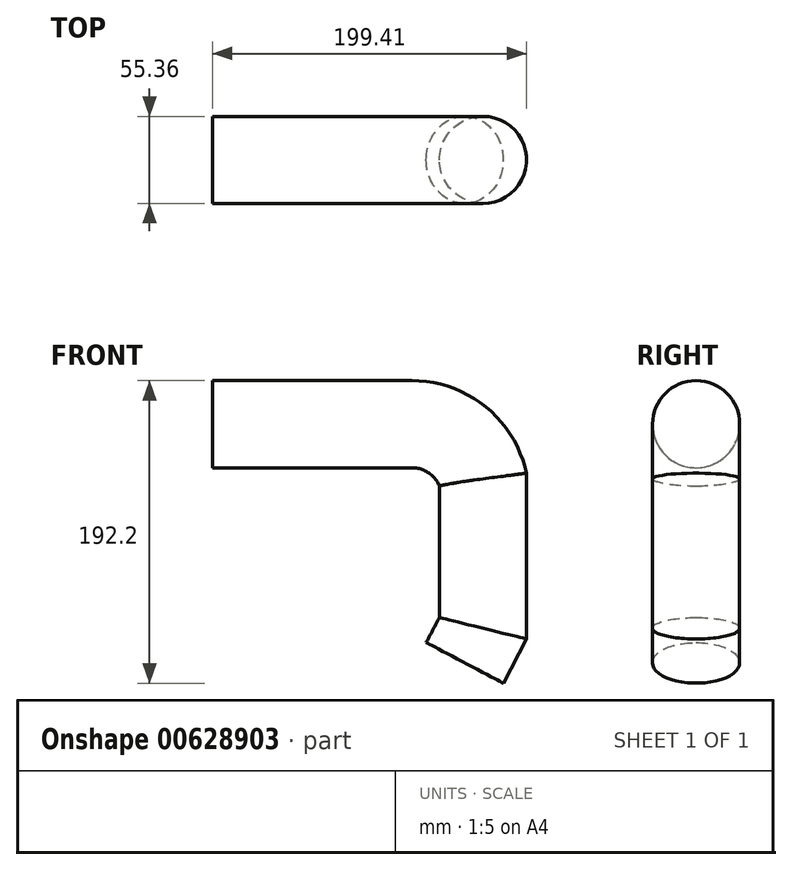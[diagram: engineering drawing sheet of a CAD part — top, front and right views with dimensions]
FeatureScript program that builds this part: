
annotation { "Feature Type Name" : "Feature", "Feature Type Description" : "" }
export const myFeature = defineFeature(function(context is Context, id is Id, definition is map)
    precondition{}
    {
        {
            var Q0;
            Q0=qCreatedBy(makeId("Front.planeOp"),FACE);
            var sketch = newSketch(context, id + "F0", { "sketchPlane" : qUnion([Q0])});
            skLineSegment(sketch, "E0", {"start": v(0, 0) * mm, "end": v(126.54, 0) * mm});
            skArc(sketch, "E1", {"start": v(171.73, -34.72) * mm, "mid": v(155.03, -9.68) * mm, "end": v(126.54, 0) * mm});
            skLineSegment(sketch, "E2", {"start": v(171.73, -34.72) * mm, "end": v(171.73, -129.64) * mm});
            skLineSegment(sketch, "E3", {"start": v(171.73, -129.64) * mm, "end": v(160.16, -151.63) * mm});
            skSolve(sketch);
        }
        {
            var Q0;
            Q0=qCreatedBy(makeId("Right.planeOp"),FACE);
            var sketch = newSketch(context, id + "F1", { "sketchPlane" : qUnion([Q0])});
            skCircle(sketch, "E4", {"center": v(0, 0) * mm, "radius": 27.68 * mm});
            skSolve(sketch);
        }
        {
            var Q0;
            Q0 = qSketchRegion(id + "F1", true);
            var Q1;
            Q1 = qConstructionFilter(qBodyType(qCreatedBy(id + "F0" ,EDGE), BodyType.WIRE), ConstructionObject.NO);
            sweep(context, id + "F2", {"profiles" : qUnion([Q0]), "path" : qUnion([Q1])});
        }
    });
